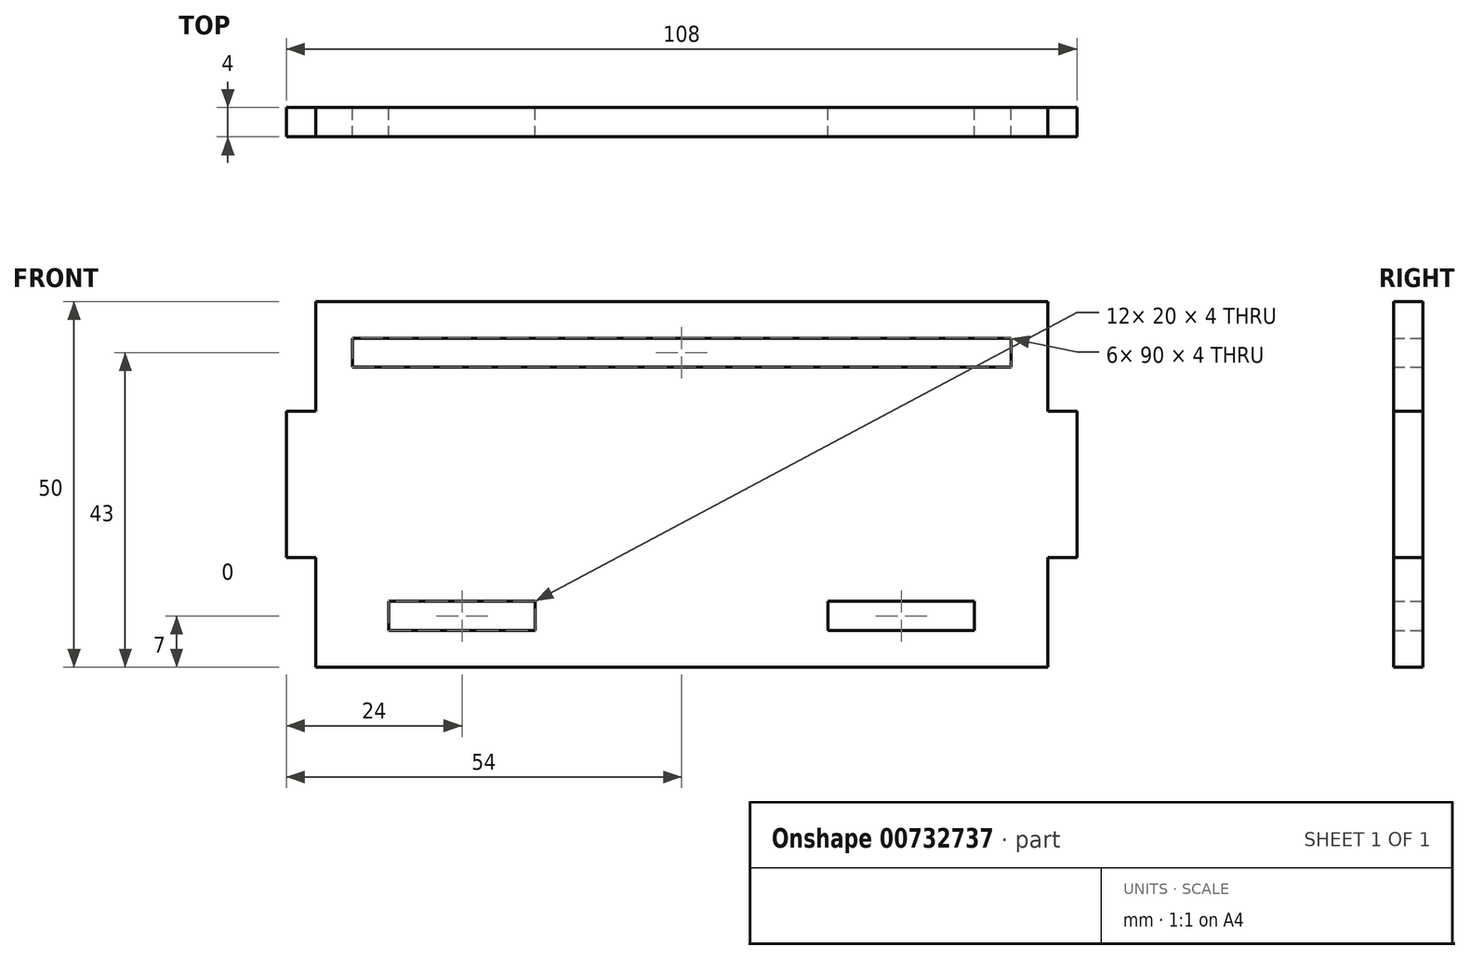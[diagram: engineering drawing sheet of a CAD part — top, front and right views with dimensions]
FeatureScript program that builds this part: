
annotation { "Feature Type Name" : "Feature", "Feature Type Description" : "" }
export const myFeature = defineFeature(function(context is Context, id is Id, definition is map)
    precondition{}
    {
        {
            var Q0;
            Q0=qCreatedBy(makeId("Front.planeOp"),FACE);
            var sketch = newSketch(context, id + "F0", { "sketchPlane" : qUnion([Q0])});
            skLineSegment(sketch, "E0.bottom", {"start": v(50, 25) * mm, "end": v(-50, 25) * mm});
            skLineSegment(sketch, "E0.top", {"start": v(50, -25) * mm, "end": v(-50, -25) * mm});
            skLineSegment(sketch, "E0.left", {"start": v(50, 25) * mm, "end": v(50, 10) * mm});
            skLineSegment(sketch, "E0.right", {"start": v(-50, 25) * mm, "end": v(-50, 10) * mm});
            skPoint(sketch, "E0.middle", {"position": v(0, 0) * mm});
            skLineSegment(sketch, "E1.bottom", {"start": v(-40, -16) * mm, "end": v(-20, -16) * mm});
            skLineSegment(sketch, "E1.top", {"start": v(-40, -20) * mm, "end": v(-20, -20) * mm});
            skLineSegment(sketch, "E1.left", {"start": v(-40, -16) * mm, "end": v(-40, -20) * mm});
            skLineSegment(sketch, "E1.right", {"start": v(-20, -16) * mm, "end": v(-20, -20) * mm});
            skLineSegment(sketch, "E2.MirrorCS", {"start": v(40, -20) * mm, "end": v(20, -20) * mm});
            skLineSegment(sketch, "E3.MirrorCS", {"start": v(40, -16) * mm, "end": v(20, -16) * mm});
            skLineSegment(sketch, "E4.MirrorCS", {"start": v(20, -16) * mm, "end": v(20, -20) * mm});
            skLineSegment(sketch, "E5.MirrorCS", {"start": v(40, -16) * mm, "end": v(40, -20) * mm});
            skLineSegment(sketch, "E6.bottom", {"start": v(-45, 20) * mm, "end": v(45, 20) * mm});
            skLineSegment(sketch, "E6.top", {"start": v(-45, 16) * mm, "end": v(45, 16) * mm});
            skLineSegment(sketch, "E6.left", {"start": v(-45, 20) * mm, "end": v(-45, 16) * mm});
            skLineSegment(sketch, "E6.right", {"start": v(45, 20) * mm, "end": v(45, 16) * mm});
            skLineSegment(sketch, "E7.bottom", {"start": v(-50, 10) * mm, "end": v(-54, 10) * mm});
            skLineSegment(sketch, "E7.top", {"start": v(-50, -10) * mm, "end": v(-54, -10) * mm});
            skLineSegment(sketch, "E7.right", {"start": v(-54, 10) * mm, "end": v(-54, -10) * mm});
            skLineSegment(sketch, "E8.trimOffspring", {"start": v(-50, -10) * mm, "end": v(-50, -25) * mm});
            skLineSegment(sketch, "E9.MirrorCS", {"start": v(50, 10) * mm, "end": v(54, 10) * mm});
            skLineSegment(sketch, "E10.MirrorCS", {"start": v(54, 10) * mm, "end": v(54, -10) * mm});
            skLineSegment(sketch, "E11.MirrorCS", {"start": v(50, -10) * mm, "end": v(54, -10) * mm});
            skLineSegment(sketch, "E12.trimOffspring", {"start": v(50, -10) * mm, "end": v(50, -25) * mm});
            skSolve(sketch);
        }
        {
            var Q0;
            Q0=qSketchRegion(id+"F0",true);
            extrude(context, id + "F1", {"entities" : qUnion([Q0]), "depth" : 4 * mm, "offsetDistance" : 25 * mm});
        }
    });
